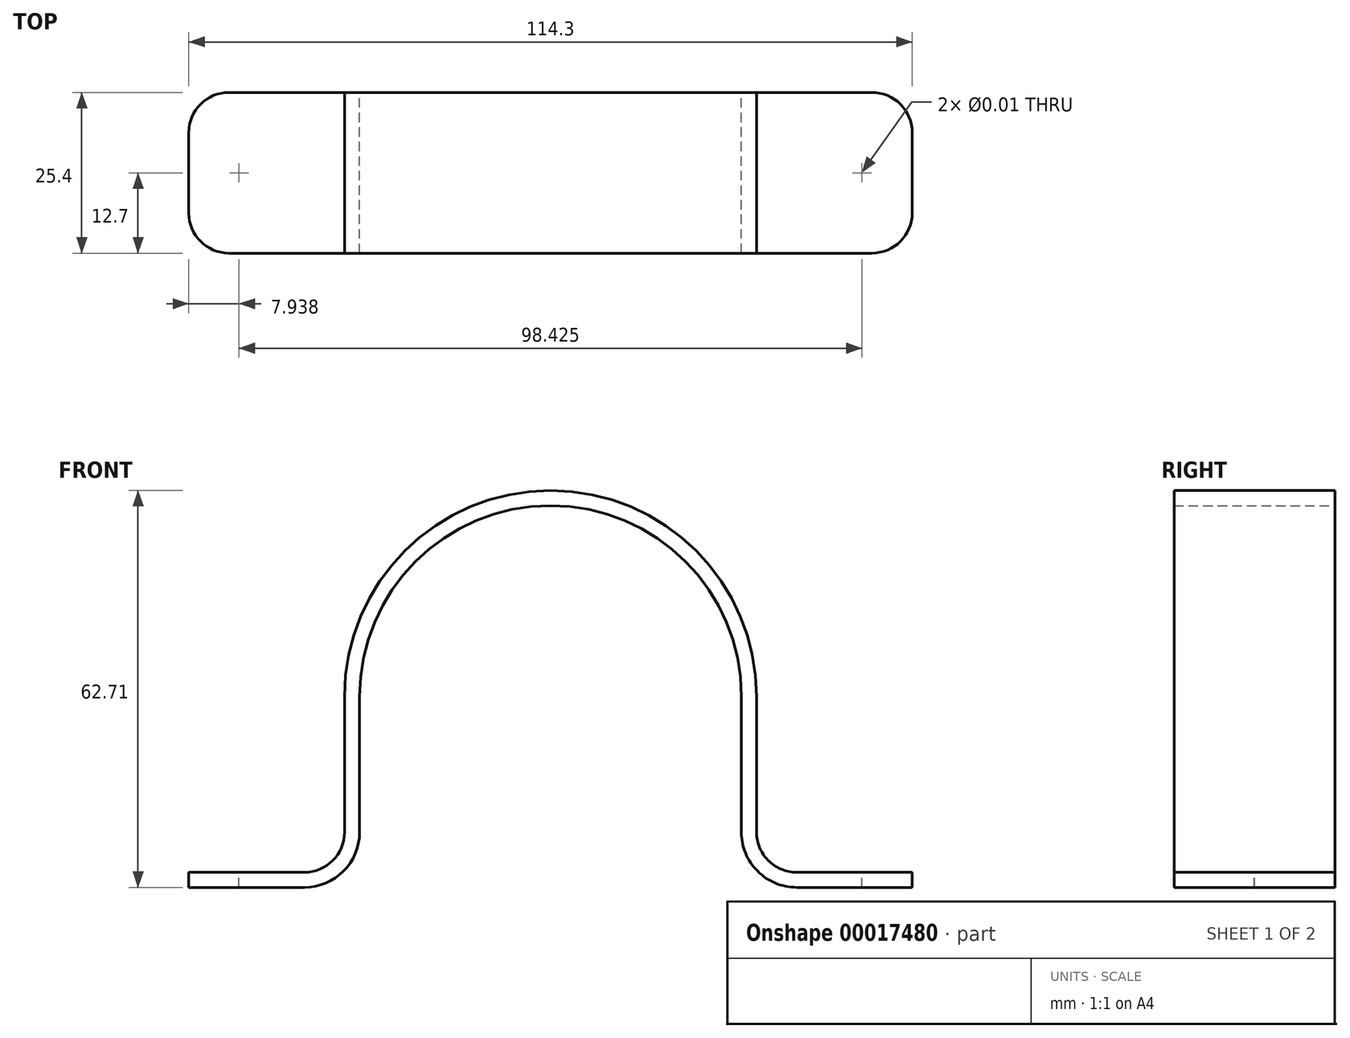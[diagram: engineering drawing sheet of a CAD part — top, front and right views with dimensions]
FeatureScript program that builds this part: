
annotation { "Feature Type Name" : "Feature", "Feature Type Description" : "" }
export const myFeature = defineFeature(function(context is Context, id is Id, definition is map)
    precondition{}
    {
        {
            var Q0;
            Q0=qCreatedBy(makeId("Front.planeOp"),FACE);
            var sketch = newSketch(context, id + "F0", { "sketchPlane" : qUnion([Q0])});
            skLineSegment(sketch, "E0", {"start": v(38.9, 0) * mm, "end": v(57.15, 0) * mm});
            skLineSegment(sketch, "E1", {"start": v(0, 0) * mm, "end": v(0, 14.89) * mm, "construction": true});
            skLineSegment(sketch, "E2.MirrorCS", {"start": v(-38.9, 0) * mm, "end": v(-57.15, 0) * mm});
            skLineSegment(sketch, "E3.MirrorCS", {"start": v(30.16, 0) * mm, "end": v(57.15, 0) * mm, "construction": true});
            skPoint(sketch, "E4.orphan", {"position": v(0, 0) * mm});
            skLineSegment(sketch, "E5", {"start": v(57.15, 0) * mm, "end": v(57.15, 2.38) * mm});
            skLineSegment(sketch, "E6.MirrorCS", {"start": v(-57.15, 0) * mm, "end": v(-57.15, 2.38) * mm});
            skArc(sketch, "E7", {"start": v(30.16, 30.16) * mm, "mid": v(0, 60.33) * mm, "end": v(-30.16, 30.16) * mm});
            skLineSegment(sketch, "E8", {"start": v(30.16, 8.73) * mm, "end": v(30.16, 30.16) * mm});
            skLineSegment(sketch, "E9.MirrorCS", {"start": v(-30.16, 8.73) * mm, "end": v(-30.16, 30.16) * mm});
            skPoint(sketch, "E10.visualSharp", {"position": v(30.16, 0) * mm});
            skArc(sketch, "E10.filletArc", {"start": v(30.16, 8.73) * mm, "mid": v(32.72, 2.56) * mm, "end": v(38.9, 0) * mm});
            skPoint(sketch, "E11.visualSharp", {"position": v(-30.16, 0) * mm});
            skArc(sketch, "E11.filletArc", {"start": v(-38.9, 0) * mm, "mid": v(-32.72, 2.56) * mm, "end": v(-30.16, 8.73) * mm});
            skLineSegment(sketch, "E12.0", {"start": v(38.9, 2.38) * mm, "end": v(57.15, 2.38) * mm});
            skArc(sketch, "E12.1", {"start": v(32.54, 8.73) * mm, "mid": v(34.4, 4.24) * mm, "end": v(38.9, 2.38) * mm});
            skLineSegment(sketch, "E12.2", {"start": v(32.54, 8.73) * mm, "end": v(32.54, 30.16) * mm});
            skArc(sketch, "E12.3", {"start": v(32.54, 30.16) * mm, "mid": v(0, 62.7) * mm, "end": v(-32.54, 30.16) * mm});
            skLineSegment(sketch, "E12.4", {"start": v(-32.54, 8.73) * mm, "end": v(-32.54, 30.16) * mm});
            skArc(sketch, "E12.5", {"start": v(-38.9, 2.38) * mm, "mid": v(-34.4, 4.24) * mm, "end": v(-32.54, 8.73) * mm});
            skLineSegment(sketch, "E12.6", {"start": v(-38.9, 2.38) * mm, "end": v(-57.15, 2.38) * mm});
            skSolve(sketch);
        }
        {
            var Q0;
            Q0 = qSketchRegion(id + "F0", true);
            extrude(context, id + "F1", {"entities" : qUnion([Q0]), "endBound" : BoundingType.SYMMETRIC, "depth" : 25.4 * mm});
        }
        {
            var Q0;
            Q0=makeQuery(id+"F1.opExtrude","CAP_EDGE",EDGE,{"disambiguationData":[OSD([sQuery(id+"F0.wireOp",EDGE,"E6.MirrorCS")])],"isStart":false});
            var Q1;
            Q1=makeQuery(id+"F1.opExtrude","CAP_EDGE",EDGE,{"disambiguationData":[OSD([sQuery(id+"F0.wireOp",EDGE,"E6.MirrorCS")])],"isStart":true});
            var Q2;
            Q2=makeQuery(id+"F1.opExtrude","CAP_EDGE",EDGE,{"disambiguationData":[OSD([sQuery(id+"F0.wireOp",EDGE,"E5")])],"isStart":false});
            var Q3;
            Q3=makeQuery(id+"F1.opExtrude","CAP_EDGE",EDGE,{"disambiguationData":[OSD([sQuery(id+"F0.wireOp",EDGE,"E5")])],"isStart":true});
            fillet(context, id + "F2", {"entities" : qUnion([Q0, Q1, Q2, Q3]), "radius" : 6.35 * mm, "tangentPropagation" : true, "allowEdgeOverflow" : false});
        }
        {
            var Q0;
            Q0=makeQuery(id+"F1.opExtrude","SWEPT_FACE",FACE,{"disambiguationData":[OSD([sQuery(id+"F0.wireOp",EDGE,"E12.0")])]});
            var sketch = newSketch(context, id + "F3", { "sketchPlane" : qUnion([Q0])});
            skLineSegment(sketch, "E13", {"start": v(0, 0) * mm, "end": v(0, 24.53) * mm, "construction": true});
            skPoint(sketch, "E14", {"position": v(49.21, 0) * mm});
            skPoint(sketch, "E15.MirrorP", {"position": v(-49.21, 0) * mm});
            skSolve(sketch);
        }
        {
            var Q0;
            Q0=sQuery(id+"F3.wireOp",VERTEX,"E15.MirrorP");
            var Q1;
            Q1=sQuery(id+"F3.wireOp",VERTEX,"E14");
            var Q2;
            Q2=makeQuery(id+"F1.opExtrude","SWEPT_BODY",BODY,{"disambiguationData":[OSD([sQuery(id+"F0.wireOp",EDGE,"cad1059e-0fe9-4170-88fc-d5843c364c94"),sQuery(id+"F0.wireOp",EDGE,"E0"),sQuery(id+"F0.wireOp",EDGE,"E2.MirrorCS"),sQuery(id+"F0.wireOp",EDGE,"0d7c21e8-ab65-49f8-a91d-79103617cbfe.0"),sQuery(id+"F0.wireOp",EDGE,"8bb09d70-fb91-4268-807e-f99b61746cdb.0"),sQuery(id+"F0.wireOp",EDGE,"fc613de7-52d6-4b80-8af3-158fa87f7a870.MirrorCS"),sQuery(id+"F0.wireOp",EDGE,"E5"),sQuery(id+"F0.wireOp",EDGE,"E6.MirrorCS")])]});
            hole(context, id + "F4", {"style" : HoleStyle.SIMPLE, "holeDiameter" : 5 / 406.4 * mm, "endStyle" : HoleEndStyle.THROUGH, "locations" : qUnion([Q0, Q1]), "scope" : qUnion([Q2])});
        }
    });
